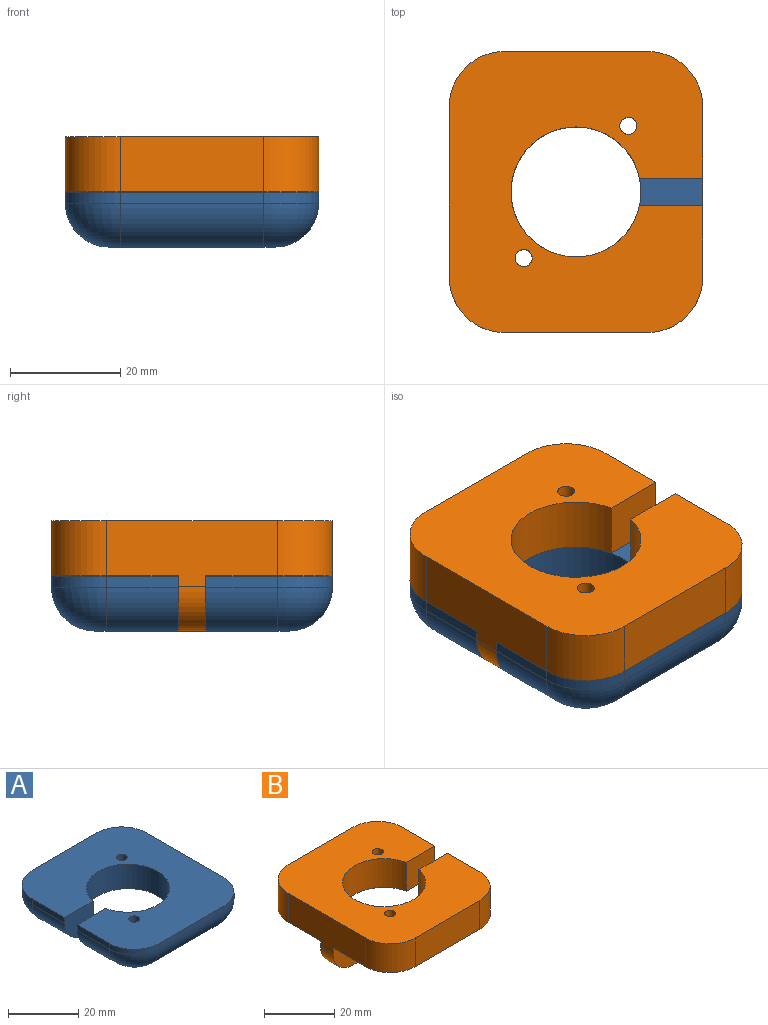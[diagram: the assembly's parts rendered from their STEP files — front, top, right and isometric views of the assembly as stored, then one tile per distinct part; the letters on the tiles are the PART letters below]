
ASSEMBLY  parts=2 mates=1
PART A: 31 faces, bbox 46x51x10 mm
  f0: plane 35x30mm, normal (0,0,-1), area 203.1mm2, adj f1,f3,f16,f17,f18,f19,f20,f21
  f1: plane 11.47x10mm, normal (0,-1,0), area 98.4mm2, adj f0,f2,f13,f15,f24,f25,f30
  f2: cylinder r=11.8mm len=23.6mm, axis (0,0,-1), area 587.4mm2, adj f1,f3,f15,f30
  f3: plane 11.47x10mm, normal (0,1,0), area 98.4mm2, adj f0,f2,f4,f15,f16,f26,f30
  f4: plane 13x2mm, normal (-1,0,0), area 26mm2, adj f3,f5,f15,f16
  f5: cylinder r=10mm len=10mm, axis (0,0,-1), area 31.4mm2, adj f4,f6,f15,f17
  f6: plane 26x2mm, normal (0,-1,0), area 52mm2, adj f5,f7,f15,f18
  f7: cylinder r=10mm len=10mm, axis (0,0,-1), area 31.4mm2, adj f6,f8,f15,f19
  f8: plane 31x2mm, normal (1,0,0), area 62mm2, adj f7,f9,f15,f20
  f9: cylinder r=10mm len=10mm, axis (0,0,-1), area 31.4mm2, adj f8,f10,f15,f21
  f10: plane 26x2mm, normal (0,1,0), area 52mm2, adj f9,f11,f15,f22
  f11: cylinder r=10mm len=10mm, axis (0,0,-1), area 31.4mm2, adj f10,f13,f15,f23
  f12: cylinder r=1.55mm len=8.5mm, axis (0,0,-1), area 82.8mm2, adj f15,f30
  f13: plane 13x2mm, normal (-1,0,0), area 26mm2, adj f1,f11,f15,f24
  f14: cylinder r=1.55mm len=8.5mm, axis (0,0,-1), area 82.8mm2, adj f15,f30
  f15: plane 51x46mm, normal (0,0,1), area 1751.2mm2, adj f1,f2,f3,f4,f5,f6,f7,f8
  f16: cylinder r=8mm len=13mm, axis (0,-1,0), area 163.4mm2, adj f0,f3,f4,f17
  f17: torus R=2mm, axis (0,0,1), area 140mm2, adj f0,f5,f16,f18
  f18: cylinder r=8mm len=26mm, axis (1,0,0), area 326.7mm2, adj f0,f6,f17,f19
  f19: torus R=2mm, axis (0,0,1), area 140mm2, adj f0,f7,f18,f20
  f20: cylinder r=8mm len=31mm, axis (0,1,0), area 389.6mm2, adj f0,f8,f19,f21
  f21: torus R=2mm, axis (0,0,1), area 140mm2, adj f0,f9,f20,f22
  f22: cylinder r=8mm len=26mm, axis (-1,0,0), area 326.7mm2, adj f0,f10,f21,f23
  f23: torus R=2mm, axis (0,0,1), area 140mm2, adj f0,f11,f22,f24
  f24: cylinder r=8mm len=13mm, axis (0,-1,0), area 163.4mm2, adj f0,f1,f13,f23
  f25: plane 13.25x1.5mm, normal (1,0,0), area 19.9mm2, adj f0,f1,f29,f30
  f26: plane 13.25x1.5mm, normal (1,0,0), area 19.9mm2, adj f0,f3,f27,f30
  f27: plane 26.5x1.5mm, normal (0,1,0), area 39.8mm2, adj f0,f26,f28,f30
  f28: plane 31.5x1.5mm, normal (-1,0,0), area 47.2mm2, adj f0,f27,f29,f30
  f29: plane 26.5x1.5mm, normal (0,-1,0), area 39.8mm2, adj f0,f25,f28,f30
  f30: plane 31.5x26.5mm, normal (0,0,-1), area 374.5mm2, adj f1,f2,f3,f12,f14,f25,f26,f27
PART B: 23 faces, bbox 46x51x20 mm
  f0: plane 11.47x10mm, normal (0,1,0), area 98.4mm2, adj f1,f2,f5,f18,f20,f21,f22
  f1: cylinder r=11.8mm len=23.6mm, axis (0,0,-1), area 733.9mm2, adj f0,f3,f10,f11,f17,f18,f19,f22
  f2: plane 5x1.75mm, normal (0,0,-1), area 8.7mm2, adj f0,f19,f20,f21
  f3: plane 46x23mm, normal (0,0,-1), area 847.4mm2, adj f1,f5,f6,f7,f8,f9,f10,f16
  f4: cylinder r=10mm len=10mm, axis (0,0,-1), area 157.1mm2, adj f5,f14,f17,f18
  f5: plane 31x12mm, normal (-1,0,0), area 320mm2, adj f0,f3,f4,f6,f17,f18,f19,f20
  f6: cylinder r=10mm len=10mm, axis (0,0,-1), area 157.1mm2, adj f3,f5,f7,f17
  f7: plane 26x10mm, normal (0,-1,0), area 260mm2, adj f3,f6,f8,f17
  f8: cylinder r=10mm len=10mm, axis (0,0,-1), area 157.1mm2, adj f3,f7,f9,f17
  f9: plane 13x10mm, normal (1,0,0), area 130mm2, adj f3,f8,f10,f17
  f10: plane 11.47x10mm, normal (0,1,0), area 114.7mm2, adj f1,f3,f9,f17
  f11: plane 11.47x10mm, normal (0,-1,0), area 114.7mm2, adj f1,f12,f17,f18
  f12: plane 13x10mm, normal (1,0,0), area 130mm2, adj f11,f13,f17,f18
  f13: cylinder r=10mm len=10mm, axis (0,0,-1), area 157.1mm2, adj f12,f14,f17,f18
  f14: plane 26x10mm, normal (0,1,0), area 260mm2, adj f4,f13,f17,f18
  f15: cylinder r=1.55mm len=10mm, axis (0,0,-1), area 97.4mm2, adj f17,f18
  f16: cylinder r=1.55mm len=10mm, axis (0,0,-1), area 97.4mm2, adj f3,f17
  f17: plane 51x46mm, normal (0,0,1), area 1751.2mm2, adj f1,f4,f5,f6,f7,f8,f9,f10
  f18: plane 46x23mm, normal (0,0,-1), area 847.4mm2, adj f0,f1,f4,f5,f11,f12,f13,f14
  f19: plane 11.47x10mm, normal (0,-1,0), area 98.4mm2, adj f1,f2,f3,f5,f20,f21,f22
  f20: cylinder r=8mm len=8mm, axis (0,-1,0), area 62.8mm2, adj f0,f2,f5,f19
  f21: plane 5x1.5mm, normal (1,0,0), area 7.5mm2, adj f0,f2,f19,f22
  f22: plane 5x1.72mm, normal (0,0,-1), area 7.7mm2, adj f0,f1,f19,f21
PLACE A t=(8.78,73.26,5.15)mm
PLACE B t=(8,73.02,15.16)mm fixed
MATE slider A.f2 <-> B.f1  axis (0,0,-1) through (8.78,73.26,10.9)mm
